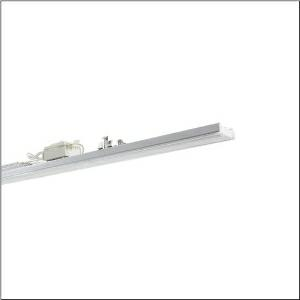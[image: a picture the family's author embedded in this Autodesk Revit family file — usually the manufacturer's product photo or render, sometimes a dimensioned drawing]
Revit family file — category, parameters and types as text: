
# Revit family: licross_r__21_recessed_ho_52te12cn4c5m_727f
name_source: partatom
category: Lighting Fixtures
units: mm (PartAtom-declared; Revit-internal decimal feet)

## family parameters
Cut with Voids When Loaded = No
Host = Face
Light Source = No
Part Type = Normal
Room Calculation Point = No
Round Connector Dimension = Use Diameter
Shared = No

## types (1)
- --- (1 x LED, 12670 lm, 68.4 W, 4000K)
    Apparent Load = 68 VA
    CIE Flux Codes = 69 91 98 100 100
    Color Rendering = 80
    Color Temperature = 4000K
    Default Elevation = 1800 mm
    Description = Licross® 21 Recessed HO, luminaire insert, of sheet steel, galvanised, coil coated, white, length: 1.500mm, width: 66mm, height: 67mm, LED rated luminous flux: 12.670lm, light colour: 840, control gear: ON/OFF Multilumen, CLOi, control gear: ECG Multilumen, with plug, 3-pole, with phase selection, mains connection: 220..240V, AC, 50/60Hz, start of lifetime: 68W, end of service life: 83W, internal wiring halogen-free, primary optical cover: cover, of PMMA, light emission: direct distribution, primary light characteristic: symmetric, protection rating (complete): IP54, insulation class (complete): insulation class I (protective earthing), certification: CE, ENEC, VDE, UKCA, protection symbol: D if used in an environment with non-conductive dust loads with corresponding accessories, impact resistance: IK06, permissible ambient temperature for indoor applications: -35..+30°C, corresponds to IFS (International Featured Standards) requirements for safety and quality in the food industry, reducing of maximum allowable ambient temperature of 5°C with ceiling mounting, LABS conformity tested according to VDMA 24364:2018-05, packaging unit: 1 piece
    Height = 58 mm
    Lamp = 1 x LED
    Lamp Light Flux = 12670 lm
    Lamp Power = 68.4 W
    Lamp count = 1
    Length = 1500 mm
    Luminous efficacy = 185 lm/W
    Manufacturer = Siteco
    ModVariant = No
    Model = 52TE12CN4C5M
    Mounting Place = Ceiling
    Mounting Type = Pendant
    Number of Poles = 1
    OnlyDefault = Yes
    Power Factor = 1
    Product Name = Licross® 21 Recessed HO
    Product group = luminaire insert | ceiling pendant
    ProductGroupID = 902
    Protection Class = Protection class I
    Protection Degree = IP 54
    RLX_Detail_Level = 1
    RLX_Emergency_Light_Flux = 0 lm
    RLX_Emergency_Type = 0
    RLX_Emergency_Type_DB = No
    RlxData = <blob elided: 22429 chars, md5=eff9250a>
    Socket = socket
    Standby Power = 0 W
    System Light Flux = 12670 lm
    System Power = 68 W
    Type Comments = factory setting: luminous flux: 100 % | (A | C | E) | 161 mA
    Type Image = l_1296930.jpg
    URL = http://relux.com
    VarID = @adj_131275
    Voltage = 0 V
    Weight = 0.00 kg
    Width = 66 mm

## geometry (parser evidence)
native form markers: Blend x4, Sweep x11
no freeform markers — native parametric forms only
